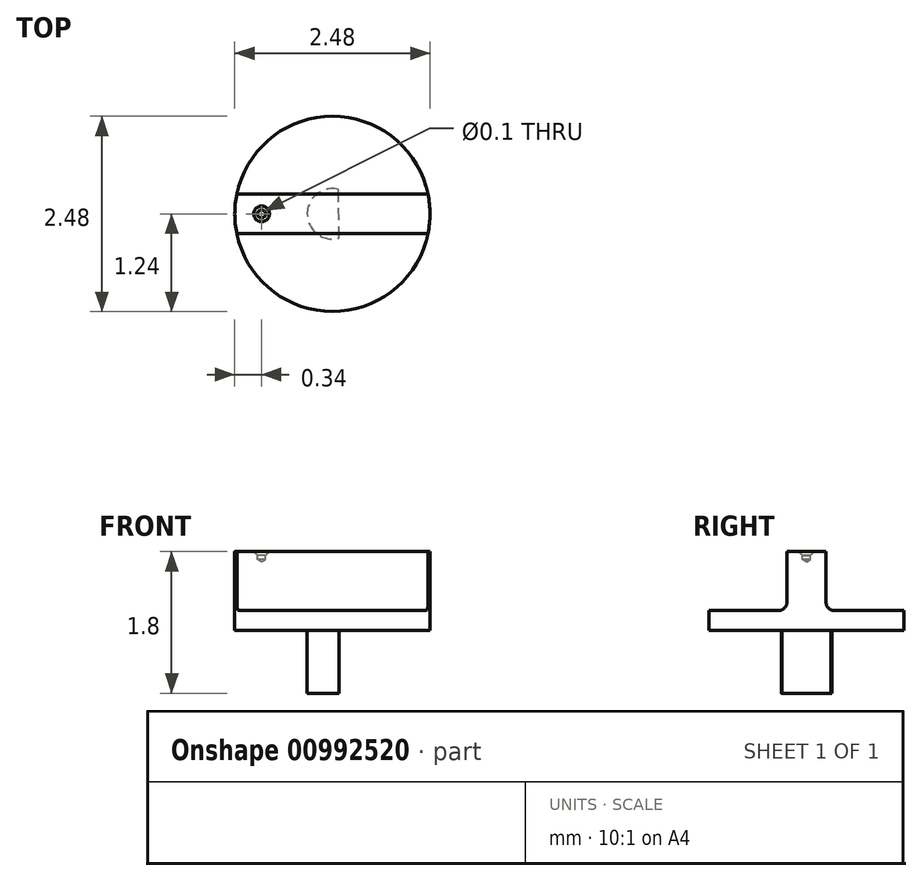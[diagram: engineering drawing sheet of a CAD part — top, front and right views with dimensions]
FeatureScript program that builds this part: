
annotation { "Feature Type Name" : "Feature", "Feature Type Description" : "" }
export const myFeature = defineFeature(function(context is Context, id is Id, definition is map)
    precondition{}
    {
        {
            var Q0;
            Q0=qCreatedBy(makeId("Top.planeOp"),FACE);
            var sketch = newSketch(context, id + "F0", { "sketchPlane" : qUnion([Q0])});
            skCircle(sketch, "E0", {"center": v(0, 0) * mm, "radius": 12.4 * mm});
            skSolve(sketch);
        }
        {
            var Q0;
            Q0=makeQuery(id+"F0.imprint","IMPRINT",FACE,{"disambiguationData":[TD([[makeQuery(id+"F0.imprint","IMPRINT",EDGE,{"derivedFrom":sQuery(id+"F0.wireOp",EDGE,"E0")}),1.0]])]});
            extrude(context, id + "F1", {"entities" : qUnion([Q0]), "depth" : 10 * mm, "offsetDistance" : 25 * mm});
        }
        {
            var Q0;
            Q0=qCreatedBy(makeId("Right.planeOp"),FACE);
            var sketch = newSketch(context, id + "F2", { "sketchPlane" : qUnion([Q0])});
            skLineSegment(sketch, "E1.bottom", {"start": v(-15, 2.5) * mm, "end": v(-2.5, 2.5) * mm});
            skLineSegment(sketch, "E1.top", {"start": v(-15, 16.57) * mm, "end": v(-2.5, 16.57) * mm});
            skLineSegment(sketch, "E1.left", {"start": v(-15, 2.5) * mm, "end": v(-15, 16.57) * mm});
            skLineSegment(sketch, "E1.right", {"start": v(-2.5, 2.5) * mm, "end": v(-2.5, 16.57) * mm});
            skLineSegment(sketch, "E2.bottom", {"start": v(-2.5, 2.5) * mm, "end": v(0, 2.5) * mm});
            skLineSegment(sketch, "E2.top", {"start": v(-2.5, 16.57) * mm, "end": v(0, 16.57) * mm});
            skLineSegment(sketch, "E2.right", {"start": v(0, 2.5) * mm, "end": v(0, 16.57) * mm});
            skLineSegment(sketch, "E3.bottom", {"start": v(0, 2.5) * mm, "end": v(2.5, 2.5) * mm});
            skLineSegment(sketch, "E3.top", {"start": v(0, 16.57) * mm, "end": v(2.5, 16.57) * mm});
            skLineSegment(sketch, "E3.right", {"start": v(2.5, 2.5) * mm, "end": v(2.5, 16.57) * mm});
            skLineSegment(sketch, "E4.bottom", {"start": v(2.5, 2.5) * mm, "end": v(15, 2.5) * mm});
            skLineSegment(sketch, "E4.top", {"start": v(2.5, 16.57) * mm, "end": v(15, 16.57) * mm});
            skLineSegment(sketch, "E4.right", {"start": v(15, 2.5) * mm, "end": v(15, 16.57) * mm});
            skSolve(sketch);
        }
        {
            var Q0;
            Q0=makeQuery(id+"F2.imprint","IMPRINT",FACE,{"disambiguationData":[TD([[makeQuery(id+"F2.imprint","IMPRINT",EDGE,{"derivedFrom":sQuery(id+"F2.wireOp",EDGE,"E4.bottom")}),1.0]])]});
            var Q1;
            Q1=makeQuery(id+"F2.imprint","IMPRINT",FACE,{"disambiguationData":[TD([[makeQuery(id+"F2.imprint","IMPRINT",EDGE,{"derivedFrom":sQuery(id+"F2.wireOp",EDGE,"E1.bottom")}),1.0]])]});
            extrude(context, id + "F3", {"entities" : qUnion([Q0, Q1]), "operationType" : NewBodyOperationType.REMOVE, "endBound" : BoundingType.SYMMETRIC, "oppositeDirection" : true, "depth" : 25 * mm, "offsetDistance" : 25 * mm});
        }
        {
            var Q0;
            Q0=makeQuery(id+"F1.opExtrude","CAP_FACE",FACE,{"disambiguationData":[OSD([sQuery(id+"F0.wireOp",EDGE,"E0")])],"isStart":false});
            var sketch = newSketch(context, id + "F4", { "sketchPlane" : qUnion([Q0])});
            skPoint(sketch, "E5", {"position": v(-9, 0) * mm});
            skSolve(sketch);
        }
        {
            var Q0;
            Q0=sQuery(id+"F4.wireOp",VERTEX,"E5");
            var Q1;
            Q1=makeQuery(id+"F1.opExtrude","SWEPT_BODY",BODY,{"disambiguationData":[OSD([sQuery(id+"F0.wireOp",EDGE,"E0")])]});
            hole(context, id + "F5", {"style" : HoleStyle.C_SINK, "endStyle" : HoleEndStyle.BLIND, "holeDiameter" : 1 * mm, "cSinkDiameter" : 2 * mm, "cSinkAngle" : 90 * degree, "majorDiameter" : 5 * mm, "holeDepth" : 1 * mm, "isTappedThrough" : true, "tappedDepth" : 12 * mm, "tapClearance" : 3, "locations" : qUnion([Q0]), "scope" : qUnion([Q1])});
        }
        {
            var Q0;
            Q0=makeQuery(id+"F1.opExtrude","CAP_FACE",FACE,{"disambiguationData":[OSD([sQuery(id+"F0.wireOp",EDGE,"E0")])],"isStart":true});
            var sketch = newSketch(context, id + "F6", { "sketchPlane" : qUnion([Q0])});
            skCircle(sketch, "E6", {"center": v(0, 0) * mm, "radius": 6.12 * mm});
            skSolve(sketch);
        }
        {
            var Q0;
            Q0=makeQuery(id+"F6.imprint","IMPRINT",FACE,{"disambiguationData":[TD([[makeQuery(id+"F6.imprint","IMPRINT",EDGE,{"derivedFrom":sQuery(id+"F6.wireOp",EDGE,"E6")}),1.0]])]});
            extrude(context, id + "F7", {"entities" : qUnion([Q0]), "operationType" : NewBodyOperationType.ADD, "depth" : 8 * mm, "offsetDistance" : 25 * mm});
        }
        {
            var Q0;
            Q0=makeQuery(id+"F7.opExtrude","CAP_FACE",FACE,{"disambiguationData":[OSD([sQuery(id+"F6.wireOp",EDGE,"E6")])],"isStart":false});
            var sketch = newSketch(context, id + "F8", { "sketchPlane" : qUnion([Q0])});
            skArc(sketch, "E7", {"start": v(0.75, -3.11) * mm, "mid": v(-3.2, 0.05) * mm, "end": v(0.85, 3.09) * mm});
            skLineSegment(sketch, "E8", {"start": v(0.85, 3.09) * mm, "end": v(0.75, -3.11) * mm});
            skSolve(sketch);
        }
        {
            var Q0;
            Q0=makeQuery(id+"F8.imprint","IMPRINT",FACE,{"disambiguationData":[TD([[makeQuery(id+"F8.imprint","IMPRINT",EDGE,{"derivedFrom":sQuery(id+"F8.wireOp",EDGE,"E7")}),-1.0]])]});
            var Q1;
            Q1=makeQuery(id+"F1.opExtrude","CAP_FACE",FACE,{"disambiguationData":[OSD([sQuery(id+"F0.wireOp",EDGE,"E0")])],"isStart":true});
            extrude(context, id + "F9", {"entities" : qUnion([Q0]), "operationType" : NewBodyOperationType.REMOVE, "endBound" : BoundingType.UP_TO_SURFACE, "oppositeDirection" : true, "depth" : 25 * mm, "endBoundEntityFace" : qUnion([Q1]), "offsetDistance" : 25 * mm});
        }
        {
            var Q0;
            Q0=makeQuery(id+"F3.boolean.opBoolean","COPY",EDGE,{"derivedFrom":makeQuery(id+"F3.opExtrude","SWEPT_EDGE",EDGE,{"disambiguationData":[OSD([sQuery(id+"F2.wireOp",EDGE,"E1.bottom"),sQuery(id+"F2.wireOp",EDGE,"E2.bottom"),sQuery(id+"F2.wireOp",EDGE,"E1.right")])]})});
            var Q1;
            Q1=makeQuery(id+"F3.boolean.opBoolean","COPY",EDGE,{"derivedFrom":makeQuery(id+"F3.opExtrude","SWEPT_EDGE",EDGE,{"disambiguationData":[OSD([sQuery(id+"F2.wireOp",EDGE,"E3.bottom"),sQuery(id+"F2.wireOp",EDGE,"E4.bottom"),sQuery(id+"F2.wireOp",EDGE,"E3.right")])]})});
            fillet(context, id + "F10", {"entities" : qUnion([Q0, Q1]), "radius" : 1 * mm, "tangentPropagation" : true, "allowEdgeOverflow" : false});
        }
        {
            var Q0;
            Q0=makeQuery(id+"F1.opExtrude","SWEPT_BODY",BODY,{"disambiguationData":[OSD([sQuery(id+"F0.wireOp",EDGE,"E0")])]});
            var Q1;
            Q1=qCreatedBy(makeId("Origin.pointOp"),VERTEX);
            transform(context, id + "F11", {"entities" : qUnion([Q0]), "transformType" : TransformType.SCALE_UNIFORMLY, "scale" : .1, "scalePoint" : qUnion([Q1]), "makeCopy" : false});
        }
    });
